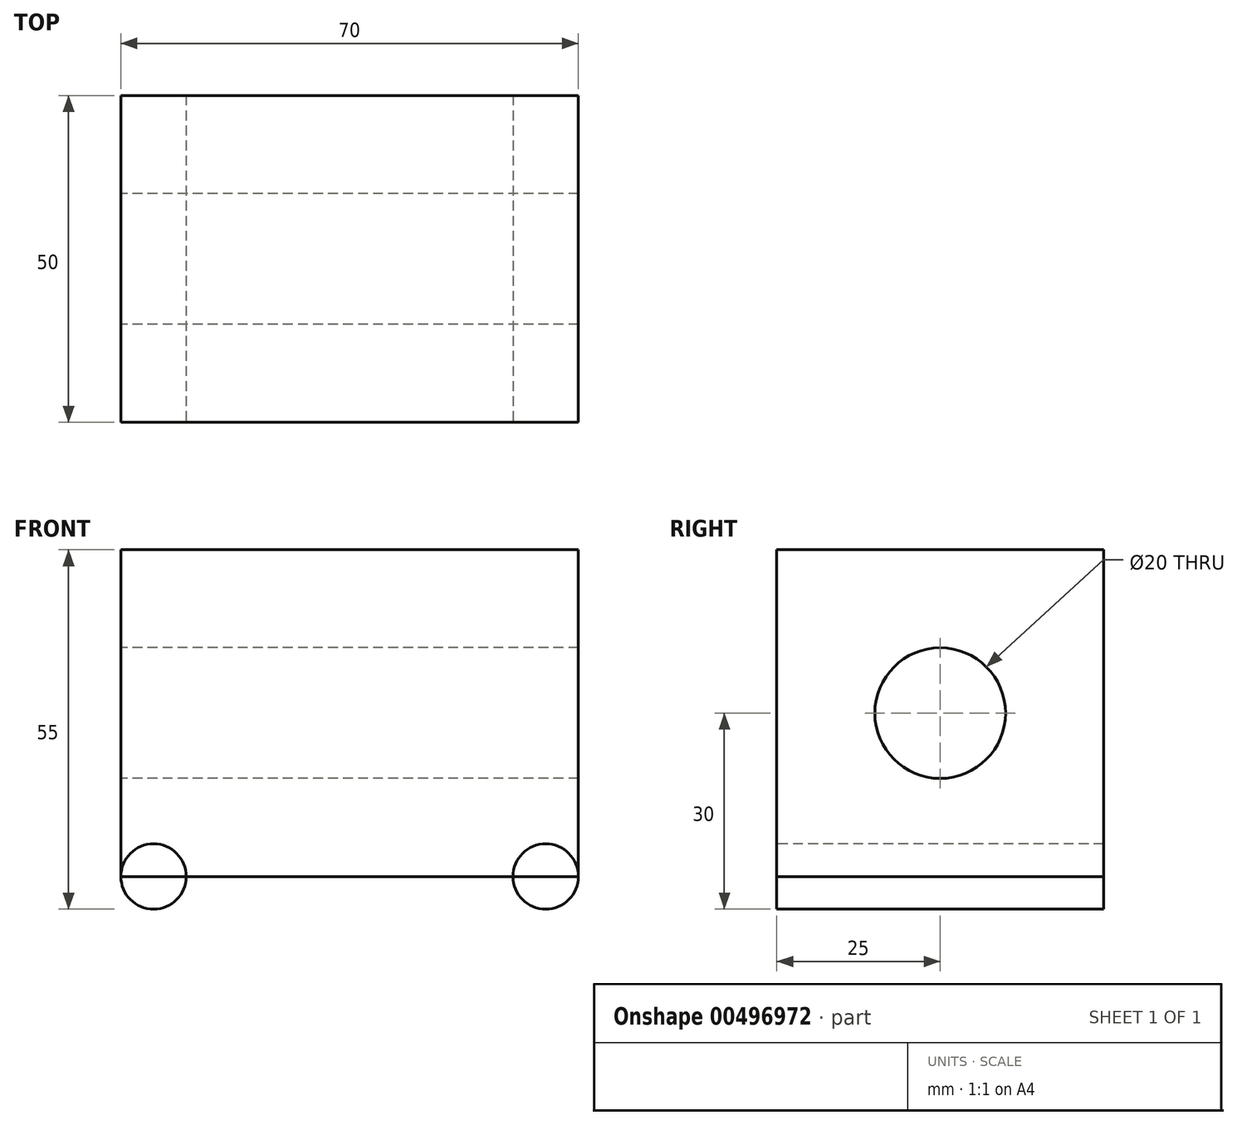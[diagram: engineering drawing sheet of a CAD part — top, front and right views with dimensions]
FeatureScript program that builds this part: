
annotation { "Feature Type Name" : "Feature", "Feature Type Description" : "" }
export const myFeature = defineFeature(function(context is Context, id is Id, definition is map)
    precondition{}
    {
        {
            var Q0;
            Q0=qCreatedBy(makeId("Front.planeOp"),FACE);
            var sketch = newSketch(context, id + "F0", { "sketchPlane" : qUnion([Q0])});
            skLineSegment(sketch, "E0.bottom", {"start": v(0, 0) * mm, "end": v(70, 0) * mm});
            skLineSegment(sketch, "E0.top", {"start": v(0, 50) * mm, "end": v(70, 50) * mm});
            skLineSegment(sketch, "E0.left", {"start": v(0, 0) * mm, "end": v(0, 50) * mm});
            skLineSegment(sketch, "E0.right", {"start": v(70, 0) * mm, "end": v(70, 50) * mm});
            skSolve(sketch);
        }
        {
            var Q0;
            Q0=qSketchRegion(id+"F0",true);
            extrude(context, id + "F1", {"entities" : qUnion([Q0]), "depth" : 50 * mm});
        }
        {
            var Q0;
            Q0=makeQuery(id+"F1.opExtrude","CAP_FACE",FACE,{"disambiguationData":[OSD([sQuery(id+"F0.wireOp",EDGE,"E0.bottom"),sQuery(id+"F0.wireOp",EDGE,"E0.top"),sQuery(id+"F0.wireOp",EDGE,"E0.left"),sQuery(id+"F0.wireOp",EDGE,"E0.right")])],"isStart":false});
            var sketch = newSketch(context, id + "F2", { "sketchPlane" : qUnion([Q0])});
            skCircle(sketch, "E1", {"center": v(5, 0) * mm, "radius": 5 * mm});
            skLineSegment(sketch, "E2", {"start": v(35, 0) * mm, "end": v(35, 12.56) * mm, "construction": true});
            skCircle(sketch, "E3.MirrorC", {"center": v(65, 0) * mm, "radius": 5 * mm});
            skSolve(sketch);
        }
        {
            var Q0;
            Q0=qSketchRegion(id+"F2",true);
            extrude(context, id + "F3", {"entities" : qUnion([Q0]), "oppositeDirection" : true, "depth" : 50 * mm});
        }
        {
            var Q0;
            Q0=makeQuery(id+"F1.opExtrude","SWEPT_FACE",FACE,{"disambiguationData":[OSD([sQuery(id+"F0.wireOp",EDGE,"E0.left")])]});
            var sketch = newSketch(context, id + "F4", { "sketchPlane" : qUnion([Q0])});
            skLineSegment(sketch, "E4", {"start": v(25, 0) * mm, "end": v(25, 25) * mm, "construction": true});
            skCircle(sketch, "E5", {"center": v(25, 25) * mm, "radius": 10 * mm});
            skSolve(sketch);
        }
        {
            var Q0;
            Q0=makeQuery(id+"F4.imprint","IMPRINT",FACE,{"disambiguationData":[TD([[makeQuery(id+"F4.imprint","IMPRINT",EDGE,{"derivedFrom":sQuery(id+"F4.wireOp",EDGE,"E5")}),1.0]])]});
            extrude(context, id + "F5", {"entities" : qUnion([Q0]), "operationType" : NewBodyOperationType.REMOVE, "endBound" : BoundingType.THROUGH_ALL, "oppositeDirection" : true, "depth" : 60 * mm});
        }
    });
